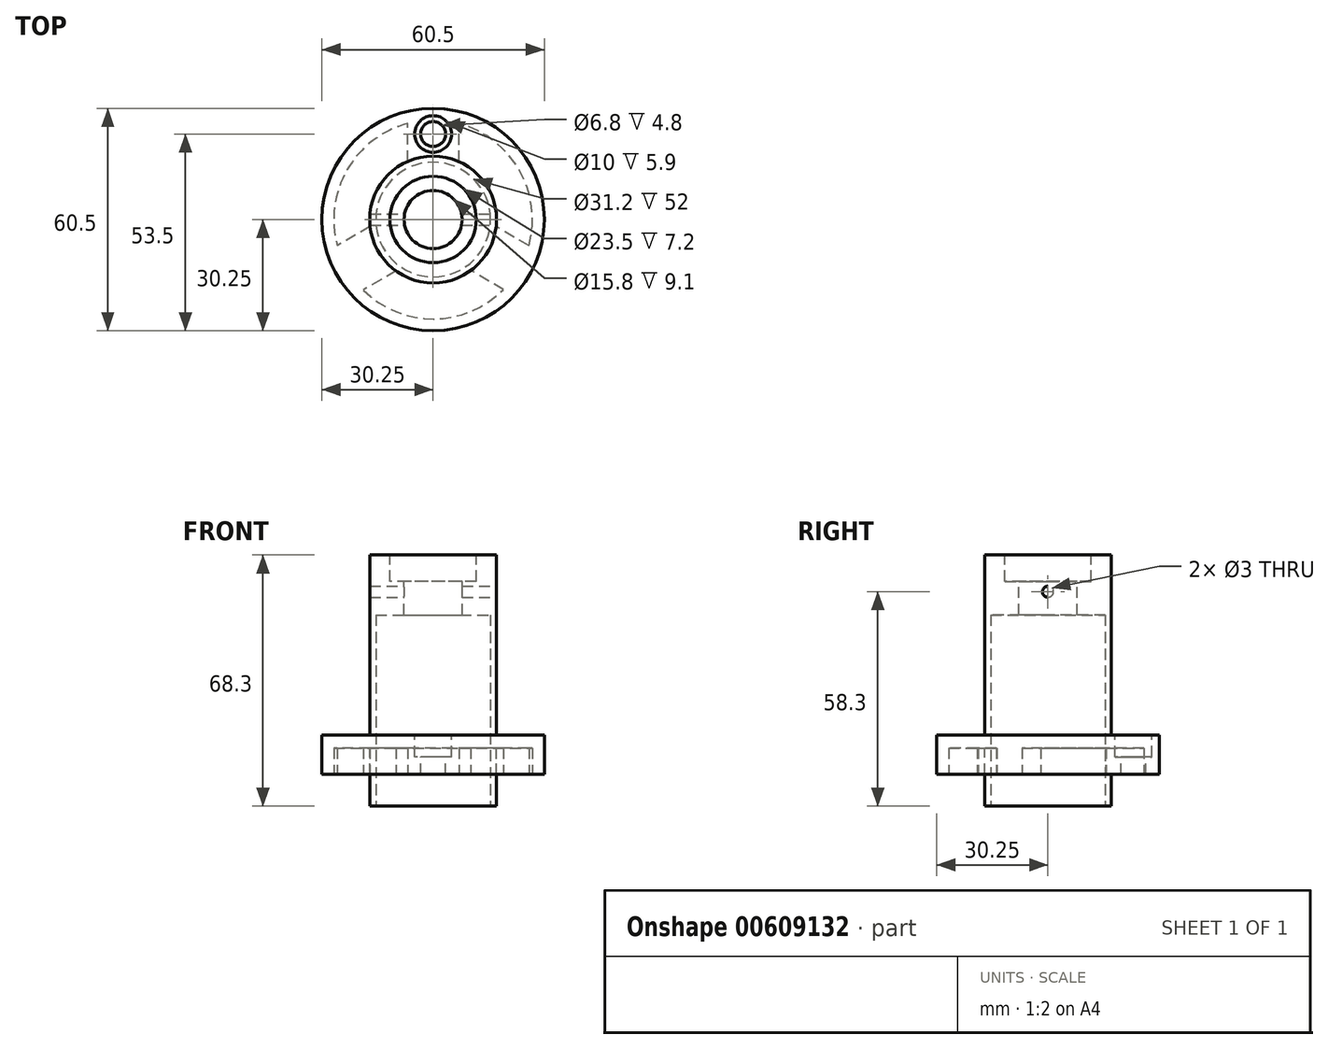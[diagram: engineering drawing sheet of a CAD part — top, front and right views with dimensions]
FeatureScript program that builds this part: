
annotation { "Feature Type Name" : "Feature", "Feature Type Description" : "" }
export const myFeature = defineFeature(function(context is Context, id is Id, definition is map)
    precondition{}
    {
        {
            var Q0;
            Q0=qCreatedBy(makeId("Front.planeOp"),FACE);
            var sketch = newSketch(context, id + "F0", { "sketchPlane" : qUnion([Q0])});
            skLineSegment(sketch, "E0", {"start": v(0, 0) * mm, "end": v(17.25, 0) * mm});
            skLineSegment(sketch, "E1", {"start": v(17.25, 0) * mm, "end": v(17.25, 8.6) * mm});
            skLineSegment(sketch, "E2", {"start": v(17.25, 8.6) * mm, "end": v(30.25, 8.6) * mm});
            skLineSegment(sketch, "E3", {"start": v(30.25, 8.6) * mm, "end": v(30.25, 19.3) * mm});
            skLineSegment(sketch, "E4", {"start": v(30.25, 19.3) * mm, "end": v(17.25, 19.3) * mm});
            skLineSegment(sketch, "E5", {"start": v(17.25, 19.3) * mm, "end": v(17.25, 68.3) * mm});
            skLineSegment(sketch, "E6", {"start": v(17.25, 68.3) * mm, "end": v(0, 68.3) * mm});
            skLineSegment(sketch, "E7", {"start": v(0, 68.3) * mm, "end": v(0, 0) * mm});
            skSolve(sketch);
        }
        {
            var Q0;
            Q0=makeQuery(id+"F0.imprint","IMPRINT",FACE,{"disambiguationData":[TD([[makeQuery(id+"F0.imprint","IMPRINT",EDGE,{"derivedFrom":sQuery(id+"F0.wireOp",EDGE,"E0")}),1.0]])]});
            var Q1;
            Q1=sQuery(id+"F0.wireOp",EDGE,"E7");
            revolve(context, id + "F1", {"entities" : qUnion([Q0]), "axis" : qUnion([Q1]), "revolveType" : RevolveType.FULL});
        }
        {
            var Q0;
            Q0=makeQuery(id+"F1.opRevolve","SWEPT_FACE",FACE,{"disambiguationData":[OSD([sQuery(id+"F0.wireOp",EDGE,"E4")])]});
            var sketch = newSketch(context, id + "F2", { "sketchPlane" : qUnion([Q0])});
            skCircle(sketch, "E8", {"center": v(0, 23.25) * mm, "radius": 3.4 * mm});
            skCircle(sketch, "E9", {"center": v(0, 23.25) * mm, "radius": 5 * mm});
            skSolve(sketch);
        }
        {
            var Q0;
            Q0=qCreatedBy(makeId("Front.planeOp"),FACE);
            var sketch = newSketch(context, id + "F3", { "sketchPlane" : qUnion([Q0])});
            skLineSegment(sketch, "E10", {"start": v(0, 77.42) * mm, "end": v(0, -26.2) * mm, "construction": true});
            skSolve(sketch);
        }
        {
            var Q0;
            Q0=makeQuery(id+"F2.imprint","IMPRINT",FACE,{"disambiguationData":[TD([[makeQuery(id+"F2.imprint","IMPRINT",EDGE,{"derivedFrom":sQuery(id+"F2.wireOp",EDGE,"E8")}),1.0]])]});
            var Q1;
            Q1=makeQuery(id+"FjlegZ9eP8M1RCN_1.2.F2.imprint","IMPRINT",FACE,{"disambiguationData":[TD([[makeQuery(id+"FjlegZ9eP8M1RCN_1.2.F2.imprint","IMPRINT",EDGE,{"derivedFrom":sQuery(id+"FjlegZ9eP8M1RCN_1.2.F2.wireOp",EDGE,"E8")}),1.0]])]});
            var Q2;
            Q2=makeQuery(id+"FjlegZ9eP8M1RCN_1.1.F2.imprint","IMPRINT",FACE,{"disambiguationData":[TD([[makeQuery(id+"FjlegZ9eP8M1RCN_1.1.F2.imprint","IMPRINT",EDGE,{"derivedFrom":sQuery(id+"FjlegZ9eP8M1RCN_1.1.F2.wireOp",EDGE,"E8")}),1.0]])]});
            extrude(context, id + "F4", {"entities" : qUnion([Q0, Q1, Q2]), "operationType" : NewBodyOperationType.REMOVE, "oppositeDirection" : true, "depth" : 25 * mm, "offsetDistance" : 25 * mm});
        }
        {
            var Q0;
            Q0=makeQuery(id+"FjlegZ9eP8M1RCN_1.2.F2.imprint","IMPRINT",FACE,{"disambiguationData":[TD([[makeQuery(id+"FjlegZ9eP8M1RCN_1.2.F2.imprint","IMPRINT",EDGE,{"derivedFrom":sQuery(id+"FjlegZ9eP8M1RCN_1.2.F2.wireOp",EDGE,"E8")}),-1.0]])]});
            var Q1;
            Q1=makeQuery(id+"FjlegZ9eP8M1RCN_1.1.F2.imprint","IMPRINT",FACE,{"disambiguationData":[TD([[makeQuery(id+"FjlegZ9eP8M1RCN_1.1.F2.imprint","IMPRINT",EDGE,{"derivedFrom":sQuery(id+"FjlegZ9eP8M1RCN_1.1.F2.wireOp",EDGE,"E8")}),-1.0]])]});
            var Q2;
            Q2=makeQuery(id+"F2.imprint","IMPRINT",FACE,{"disambiguationData":[TD([[makeQuery(id+"F2.imprint","IMPRINT",EDGE,{"derivedFrom":sQuery(id+"F2.wireOp",EDGE,"E8")}),-1.0]])]});
            extrude(context, id + "F5", {"entities" : qUnion([Q0, Q1, Q2]), "operationType" : NewBodyOperationType.REMOVE, "oppositeDirection" : true, "depth" : 5.9 * mm, "offsetDistance" : 25 * mm});
        }
        {
            var Q0;
            Q0=makeQuery(id+"F1.opRevolve","SWEPT_FACE",FACE,{"disambiguationData":[OSD([sQuery(id+"F0.wireOp",EDGE,"E2")])]});
            var sketch = newSketch(context, id + "F6", { "sketchPlane" : qUnion([Q0])});
            skArc(sketch, "E11", {"start": v(19.18, 19.04) * mm, "mid": v(-23.4, -13.51) * mm, "end": v(26.08, 7.09) * mm});
            skLineSegment(sketch, "E12", {"start": v(19.18, 19.04) * mm, "end": v(10.2, 13.86) * mm});
            skLineSegment(sketch, "E13.MirrorCS", {"start": v(26.08, 7.09) * mm, "end": v(17.1, 1.9) * mm});
            skLineSegment(sketch, "E14", {"start": v(-10.06, 14) * mm, "end": v(-19.03, 19.18) * mm});
            skLineSegment(sketch, "E15", {"start": v(-17.14, 1.93) * mm, "end": v(-26.08, 7.09) * mm});
            skLineSegment(sketch, "E16", {"start": v(-6.9, -15.8) * mm, "end": v(-6.9, -26.13) * mm});
            skLineSegment(sketch, "E17", {"start": v(7.1, -15.72) * mm, "end": v(7.1, -26.07) * mm});
            skSolve(sketch);
        }
        {
            var Q0;
            {var subQ3=sQuery(id+"F6.wireOp",EDGE,"E14");Q0=makeQuery(id+"F6.imprint","IMPRINT",FACE,{"disambiguationData":[TD([[makeQuery(id+"F6.imprint","IMPRINT",EDGE,{"derivedFrom":subQ3}),-1.0]])]});}
            var Q1;
            {var subQ0=sQuery(id+"F6.wireOp",EDGE,"E15");Q1=makeQuery(id+"F6.imprint","IMPRINT",FACE,{"disambiguationData":[TD([[makeQuery(id+"F6.imprint","IMPRINT",EDGE,{"derivedFrom":subQ0}),1.0]])]});}
            var Q2;
            {var subQ3=sQuery(id+"F6.wireOp",EDGE,"E17");Q2=makeQuery(id+"F6.imprint","IMPRINT",FACE,{"disambiguationData":[TD([[makeQuery(id+"F6.imprint","IMPRINT",EDGE,{"derivedFrom":subQ3}),1.0]])]});}
            extrude(context, id + "F7", {"entities" : qUnion([Q0, Q1, Q2]), "operationType" : NewBodyOperationType.REMOVE, "oppositeDirection" : true, "depth" : 7.2 * mm, "offsetDistance" : 25 * mm});
        }
        {
            var Q0;
            Q0=makeQuery(id+"F1.opRevolve","SWEPT_FACE",FACE,{"disambiguationData":[OSD([sQuery(id+"F0.wireOp",EDGE,"E0")])]});
            var sketch = newSketch(context, id + "F8", { "sketchPlane" : qUnion([Q0])});
            skCircle(sketch, "E18", {"center": v(0, 0) * mm, "radius": 15.6 * mm});
            skSolve(sketch);
        }
        {
            var Q0;
            Q0=makeQuery(id+"F8.imprint","IMPRINT",FACE,{"disambiguationData":[TD([[makeQuery(id+"F8.imprint","IMPRINT",EDGE,{"derivedFrom":sQuery(id+"F8.wireOp",EDGE,"E18")}),1.0]])]});
            extrude(context, id + "F9", {"entities" : qUnion([Q0]), "operationType" : NewBodyOperationType.REMOVE, "oppositeDirection" : true, "depth" : 52 * mm, "offsetDistance" : 25 * mm});
        }
        {
            var Q0;
            Q0=makeQuery(id+"F1.opRevolve","SWEPT_FACE",FACE,{"disambiguationData":[OSD([sQuery(id+"F0.wireOp",EDGE,"E6")])]});
            var sketch = newSketch(context, id + "F10", { "sketchPlane" : qUnion([Q0])});
            skCircle(sketch, "E19", {"center": v(0, 0) * mm, "radius": 11.75 * mm});
            skCircle(sketch, "E20", {"center": v(0, 0) * mm, "radius": 7.9 * mm});
            skSolve(sketch);
        }
        {
            var Q0;
            Q0=makeQuery(id+"F10.imprint","IMPRINT",FACE,{"disambiguationData":[TD([[makeQuery(id+"F10.imprint","IMPRINT",EDGE,{"derivedFrom":sQuery(id+"F10.wireOp",EDGE,"E19")}),1.0]])]});
            extrude(context, id + "F11", {"entities" : qUnion([Q0]), "operationType" : NewBodyOperationType.REMOVE, "oppositeDirection" : true, "depth" : 7.2 * mm, "offsetDistance" : 25 * mm});
        }
        {
            var Q0;
            Q0=makeQuery(id+"F11.boolean.opBoolean","SPLIT",FACE,{"disambiguationData":[TD([makeQuery(id+"F11.opExtrude","SWEPT_FACE",FACE,{"disambiguationData":[OSD([sQuery(id+"F10.wireOp",EDGE,"E20")])]})])],"derivedFrom":makeQuery(id+"F1.opRevolve","SWEPT_FACE",FACE,{"disambiguationData":[OSD([sQuery(id+"F0.wireOp",EDGE,"E6")])]})});
            extrude(context, id + "F12", {"entities" : qUnion([Q0]), "operationType" : NewBodyOperationType.REMOVE, "oppositeDirection" : true, "depth" : 97.5 * mm, "offsetDistance" : 25 * mm});
        }
        {
            var Q0;
            Q0=qCreatedBy(makeId("Right.planeOp"),FACE);
            var sketch = newSketch(context, id + "F13", { "sketchPlane" : qUnion([Q0])});
            skCircle(sketch, "E21", {"center": v(0, 58.3) * mm, "radius": 1.5 * mm});
            skSolve(sketch);
        }
        {
            var Q0;
            Q0 = qSketchRegion(id + "F13", true);
            extrude(context, id + "F14", {"entities" : qUnion([Q0]), "operationType" : NewBodyOperationType.REMOVE, "endBound" : BoundingType.SYMMETRIC, "oppositeDirection" : true, "depth" : 65 * mm, "offsetDistance" : 25 * mm});
        }
    });
